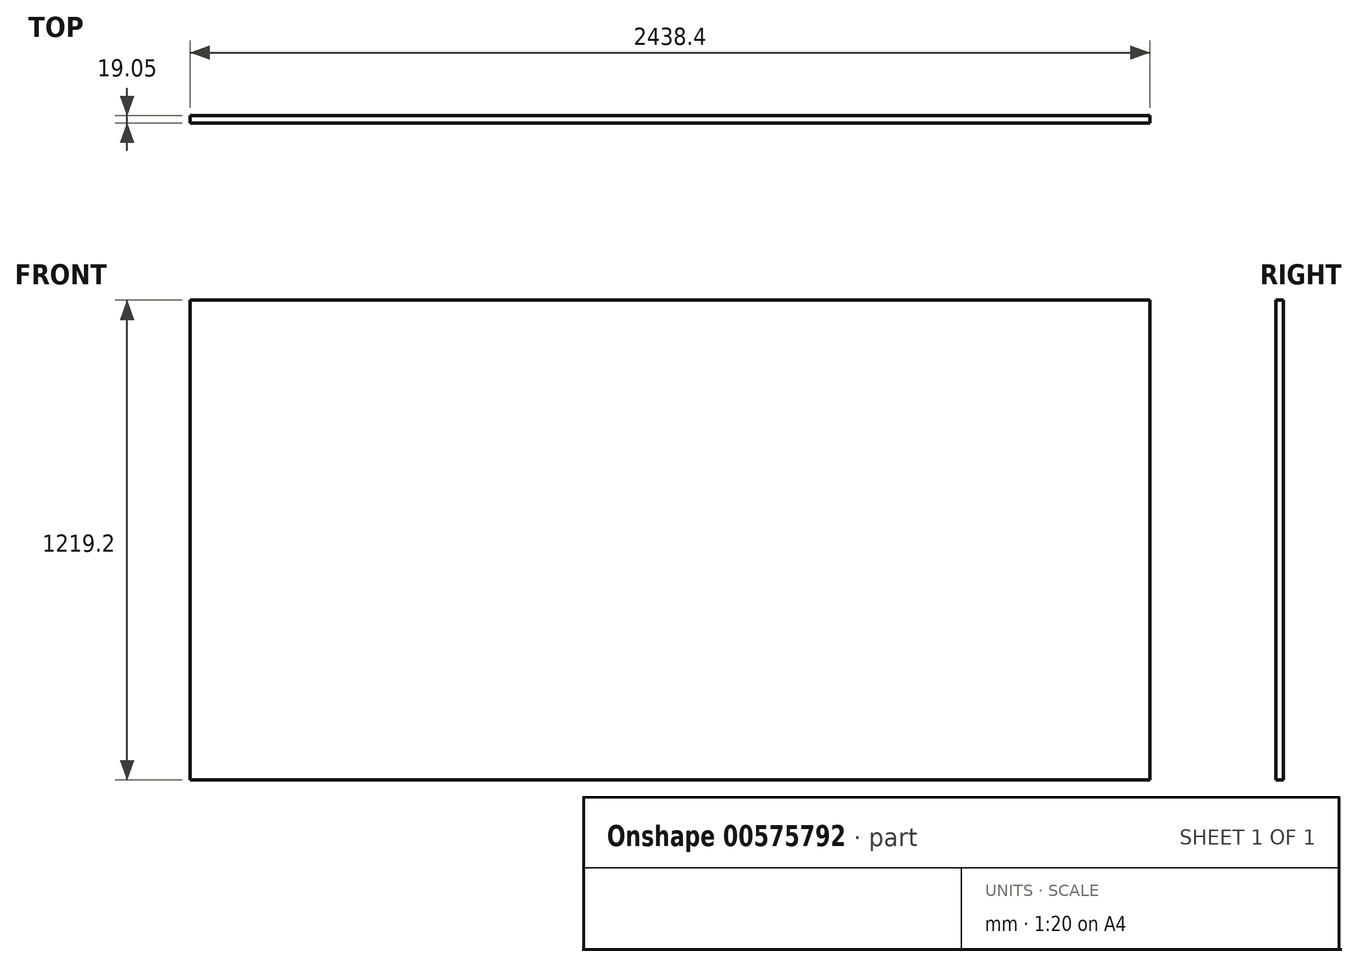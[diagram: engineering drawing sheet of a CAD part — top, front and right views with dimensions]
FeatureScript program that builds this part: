
annotation { "Feature Type Name" : "Feature", "Feature Type Description" : "" }
export const myFeature = defineFeature(function(context is Context, id is Id, definition is map)
    precondition{}
    {
        {
            var Q0;
            Q0=qCreatedBy(makeId("Front.planeOp"),FACE);
            var sketch = newSketch(context, id + "F0", { "sketchPlane" : qUnion([Q0])});
            skLineSegment(sketch, "E0", {"start": v(-1205.13, 616.35) * mm, "end": v(1233.27, 616.35) * mm});
            skLineSegment(sketch, "E1", {"start": v(1233.27, 616.35) * mm, "end": v(1233.27, -602.85) * mm});
            skLineSegment(sketch, "E2", {"start": v(1233.27, -602.85) * mm, "end": v(-1205.13, -602.85) * mm});
            skLineSegment(sketch, "E3", {"start": v(-1205.13, -602.85) * mm, "end": v(-1205.13, 616.35) * mm});
            skSolve(sketch);
        }
        {
            var Q0;
            Q0=qSketchRegion(id+"F0",true);
            extrude(context, id + "F1", {"entities" : qUnion([Q0]), "depth" : 19.05 * mm, "offsetDistance" : 30.48 * mm});
        }
    });
